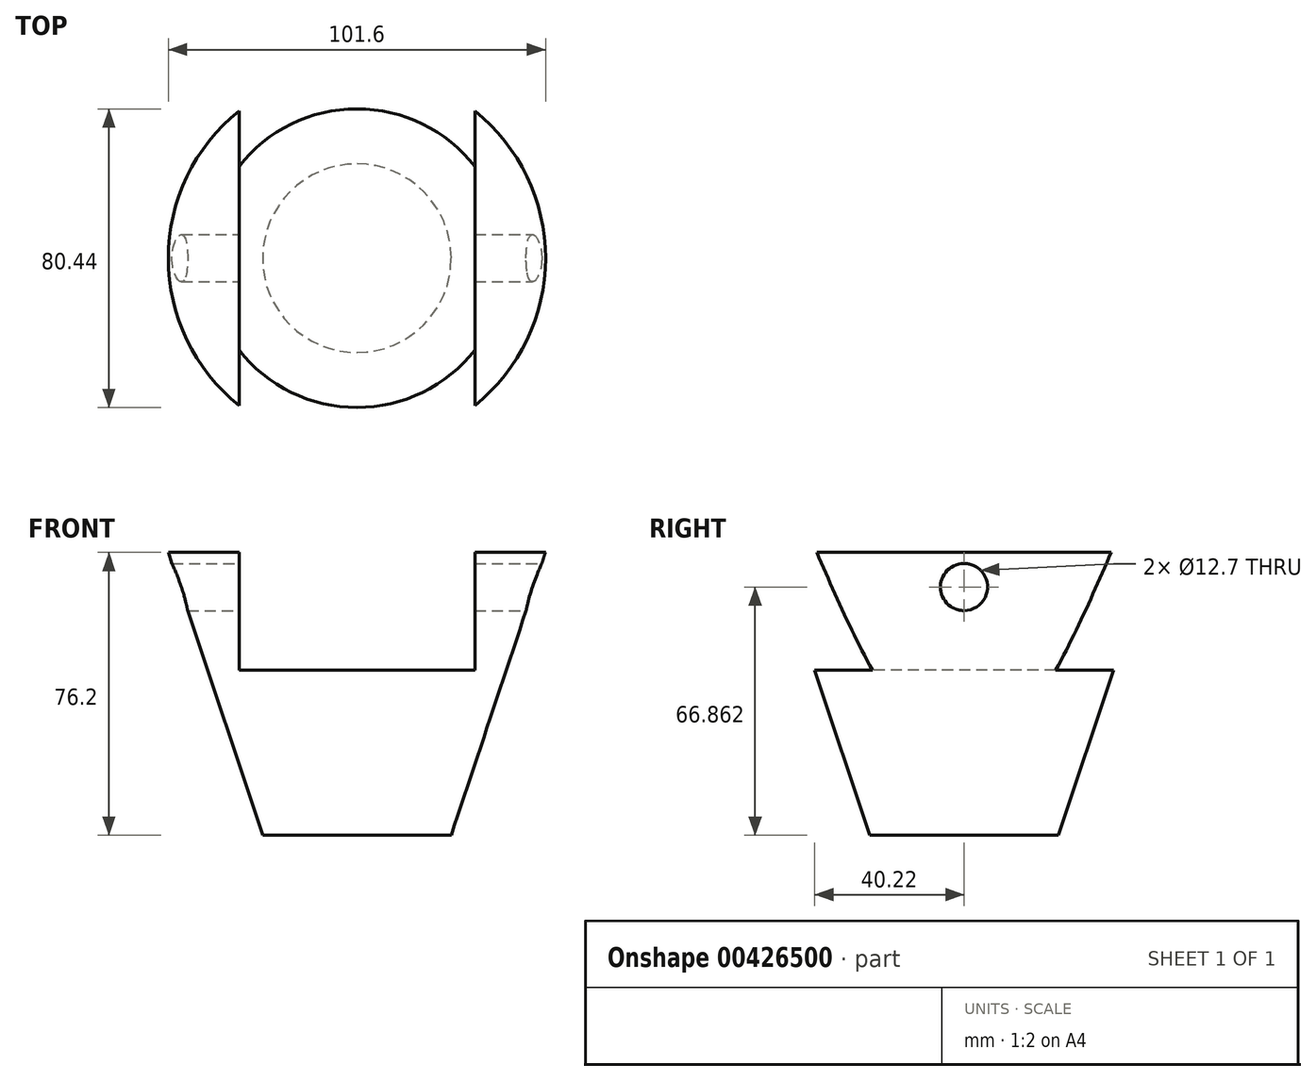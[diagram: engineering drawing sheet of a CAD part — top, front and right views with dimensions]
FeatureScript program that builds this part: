
annotation { "Feature Type Name" : "Feature", "Feature Type Description" : "" }
export const myFeature = defineFeature(function(context is Context, id is Id, definition is map)
    precondition{}
    {
        {
            var Q0;
            Q0=qCreatedBy(makeId("Top.planeOp"),FACE);
            var sketch = newSketch(context, id + "F0", { "sketchPlane" : qUnion([Q0])});
            skCircle(sketch, "E0", {"center": v(0, 0) * mm, "radius": 25.4 * mm});
            skSolve(sketch);
        }
        {
            var Q0;
            Q0=qCreatedBy(makeId("Top.planeOp"),FACE);
            cPlane(context, id + "F1", {"entities" : qUnion([Q0]), "cplaneType" : CPlaneType.OFFSET, "offset" : 76.2 * mm, "width" : 152.4 * mm, "height" : 152.4 * mm});
        }
        {
            var Q0;
            Q0=qCreatedBy(id+"F1.planeOp",FACE);
            var sketch = newSketch(context, id + "F2", { "sketchPlane" : qUnion([Q0])});
            skCircle(sketch, "E1", {"center": v(0, 0) * mm, "radius": 50.8 * mm});
            skSolve(sketch);
        }
        {
            var Q0;
            Q0=makeQuery(id+"F0.imprint","IMPRINT",FACE,{"disambiguationData":[TD([[makeQuery(id+"F0.imprint","IMPRINT",EDGE,{"derivedFrom":sQuery(id+"F0.wireOp",EDGE,"E0")}),1.0]])]});
            var Q1;
            Q1=makeQuery(id+"F2.imprint","IMPRINT",FACE,{"disambiguationData":[TD([[makeQuery(id+"F2.imprint","IMPRINT",EDGE,{"derivedFrom":sQuery(id+"F2.wireOp",EDGE,"E1")}),1.0]])]});
            loft(context, id + "F3", {"sheetProfilesArray" : [{ "sheetProfileEntities" : qUnion([Q0]) }, { "sheetProfileEntities" : qUnion([Q1]) }]});
        }
        {
            var Q0;
            Q0=makeQuery(id+"F3.opLoft","CAP_FACE",FACE,{"disambiguationData":[OSD([makeQuery(id+"F2.imprint","IMPRINT",FACE,{"disambiguationData":[TD([[makeQuery(id+"F2.imprint","IMPRINT",EDGE,{"derivedFrom":sQuery(id+"F2.wireOp",EDGE,"E1")}),1.0]])]})])],"isStart":true});
            var sketch = newSketch(context, id + "F4", { "sketchPlane" : qUnion([Q0])});
            skLineSegment(sketch, "E2.bottom", {"start": v(31.75, 75.12) * mm, "end": v(-31.75, 75.12) * mm});
            skLineSegment(sketch, "E2.top", {"start": v(31.75, -75.12) * mm, "end": v(-31.75, -75.12) * mm});
            skLineSegment(sketch, "E2.left", {"start": v(31.75, 75.12) * mm, "end": v(31.75, -75.12) * mm});
            skLineSegment(sketch, "E2.right", {"start": v(-31.75, 75.12) * mm, "end": v(-31.75, -75.12) * mm});
            skPoint(sketch, "E2.middle", {"position": v(0, 0) * mm});
            skSolve(sketch);
        }
        {
            var Q0;
            {var subQ0=sQuery(id+"F4.wireOp",EDGE,"E2.left");var subQ1=makeQuery(id+"F3.opLoft","MID_CAP_EDGE",EDGE,{"disambiguationData":[OSD([sQuery(id+"F0.wireOp",EDGE,"E0"),sQuery(id+"F2.wireOp",EDGE,"E1")])],"capPos":1.0});var subQ2=makeQuery(id+"F4.imprint","INTERSECT",VERTEX,{"disambiguationData":[OD(0.0)],"derivedFrom":[subQ1,subQ0]});Q0=makeQuery(id+"F4.imprint","IMPRINT",FACE,{"disambiguationData":[TD([[makeQuery(id+"F4.imprint","IMPRINT",EDGE,{"disambiguationData":[TD([[subQ2,-1.0]])],"derivedFrom":subQ0}),-1.0]])]});}
            var Q1;
            Q1 = qSketchRegion(id + "F7", true);
            extrude(context, id + "F5", {"entities" : qUnion([Q0, Q1]), "operationType" : NewBodyOperationType.REMOVE, "oppositeDirection" : true, "depth" : 31.75 * mm});
        }
        {
            var Q0;
            Q0=qCreatedBy(makeId("Right.planeOp"),FACE);
            cPlane(context, id + "F6", {"entities" : qUnion([Q0]), "cplaneType" : CPlaneType.OFFSET, "offset" : 50.8 * mm, "width" : 152.4 * mm, "height" : 152.4 * mm});
        }
        {
            var Q0;
            Q0=qCreatedBy(id+"F6.planeOp",FACE);
            var sketch = newSketch(context, id + "F7", { "sketchPlane" : qUnion([Q0])});
            skCircle(sketch, "E3", {"center": v(0, 66.86) * mm, "radius": 6.35 * mm});
            skLineSegment(sketch, "E4", {"start": v(0, 0) * mm, "end": v(0, 45.32) * mm, "construction": true});
            skLineSegment(sketch, "E5", {"start": v(0, 45.32) * mm, "end": v(0, 66.86) * mm, "construction": true});
            skSolve(sketch);
        }
        {
            var Q0;
            Q0=makeQuery(id+"F7.imprint","IMPRINT",FACE,{"disambiguationData":[TD([[makeQuery(id+"F7.imprint","IMPRINT",EDGE,{"derivedFrom":sQuery(id+"F7.wireOp",EDGE,"E3")}),1.0]])]});
            extrude(context, id + "F8", {"entities" : qUnion([Q0]), "operationType" : NewBodyOperationType.REMOVE, "oppositeDirection" : true, "depth" : 127 * mm});
        }
    });
